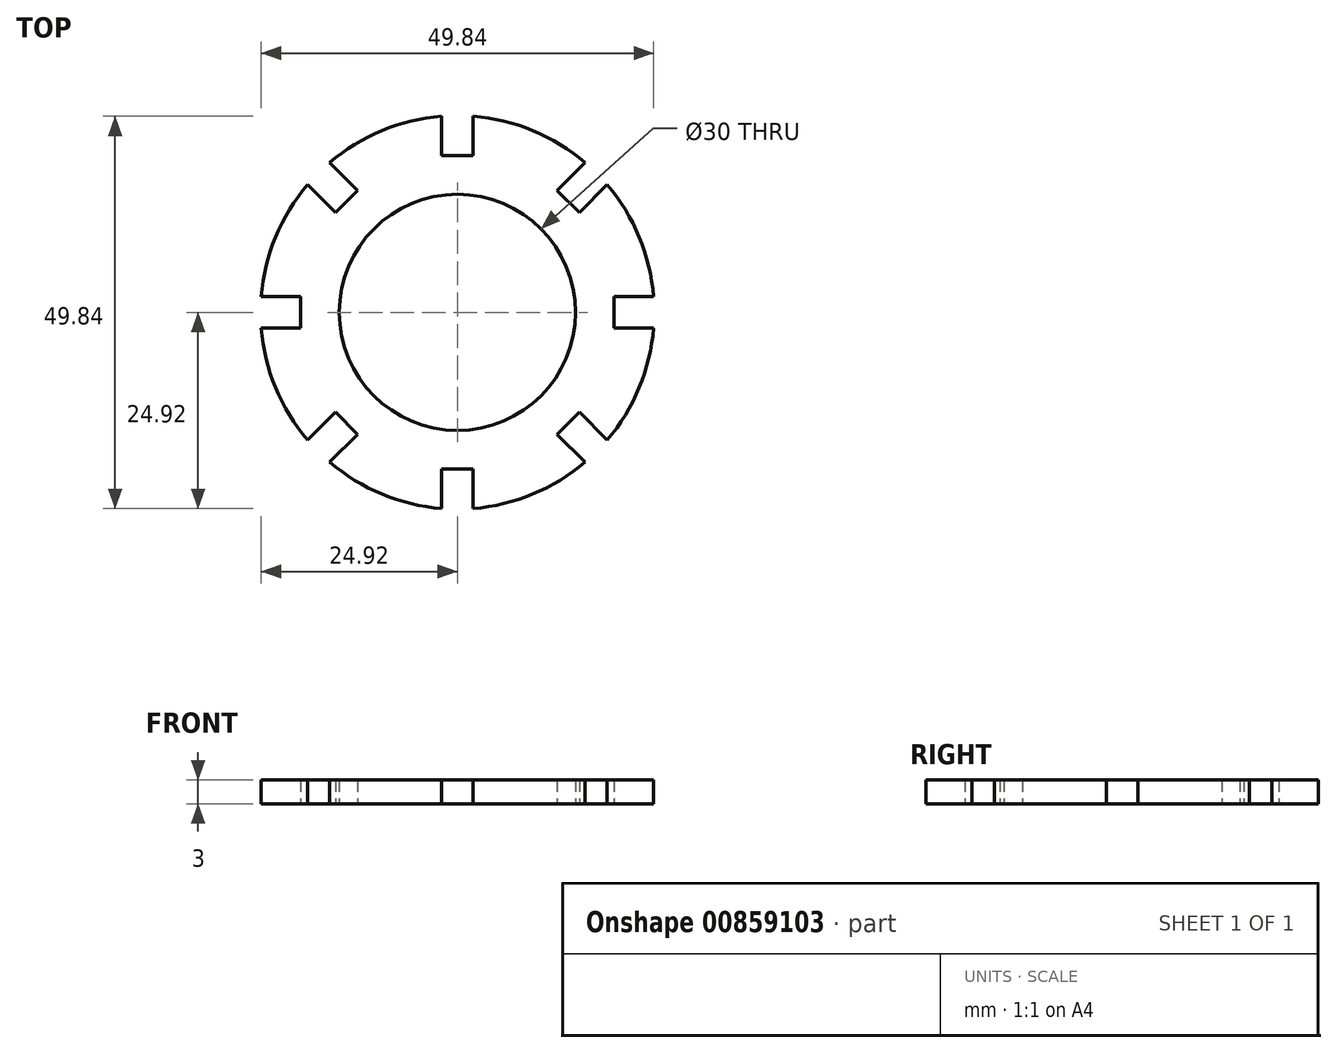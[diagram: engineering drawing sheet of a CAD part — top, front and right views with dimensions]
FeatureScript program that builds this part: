
annotation { "Feature Type Name" : "Feature", "Feature Type Description" : "" }
export const myFeature = defineFeature(function(context is Context, id is Id, definition is map)
    precondition{}
    {
        {
            var Q0;
            Q0=qCreatedBy(makeId("Top.planeOp"),FACE);
            var sketch = newSketch(context, id + "F0", { "sketchPlane" : qUnion([Q0])});
            skCircle(sketch, "E0", {"center": v(0, 0) * mm, "radius": 25 * mm});
            skCircle(sketch, "E1", {"center": v(0, 0) * mm, "radius": 15 * mm});
            skLineSegment(sketch, "E2", {"start": v(0, -19.92) * mm, "end": v(2, -19.92) * mm});
            skLineSegment(sketch, "E3", {"start": v(2, -19.92) * mm, "end": v(0, -19.92) * mm});
            skLineSegment(sketch, "E4", {"start": v(0, -19.92) * mm, "end": v(-2, -19.92) * mm});
            skLineSegment(sketch, "E5", {"start": v(-2, -19.92) * mm, "end": v(-2, -24.92) * mm});
            skLineSegment(sketch, "E6", {"start": v(2, -19.92) * mm, "end": v(2, -24.92) * mm});
            skLineSegment(sketch, "E7.1.0", {"start": v(12.67, -15.5) * mm, "end": v(16.2, -19.04) * mm});
            skLineSegment(sketch, "E7.1.1", {"start": v(14.09, -14.09) * mm, "end": v(12.67, -15.5) * mm});
            skLineSegment(sketch, "E7.1.2", {"start": v(15.5, -12.67) * mm, "end": v(14.09, -14.09) * mm});
            skLineSegment(sketch, "E7.1.3", {"start": v(15.5, -12.67) * mm, "end": v(19.04, -16.2) * mm});
            skLineSegment(sketch, "E7.2.0", {"start": v(19.92, -2) * mm, "end": v(24.92, -2) * mm});
            skLineSegment(sketch, "E7.2.1", {"start": v(19.92, 0) * mm, "end": v(19.92, -2) * mm});
            skLineSegment(sketch, "E7.2.2", {"start": v(19.92, 2) * mm, "end": v(19.92, 0) * mm});
            skLineSegment(sketch, "E7.2.3", {"start": v(19.92, 2) * mm, "end": v(24.92, 2) * mm});
            skLineSegment(sketch, "E7.3.0", {"start": v(15.5, 12.67) * mm, "end": v(19.04, 16.2) * mm});
            skLineSegment(sketch, "E7.3.1", {"start": v(14.09, 14.09) * mm, "end": v(15.5, 12.67) * mm});
            skLineSegment(sketch, "E7.3.2", {"start": v(12.67, 15.5) * mm, "end": v(14.09, 14.09) * mm});
            skLineSegment(sketch, "E7.3.3", {"start": v(12.67, 15.5) * mm, "end": v(16.2, 19.04) * mm});
            skLineSegment(sketch, "E7.4.0", {"start": v(2, 19.92) * mm, "end": v(2, 24.92) * mm});
            skLineSegment(sketch, "E7.4.1", {"start": v(0, 19.92) * mm, "end": v(2, 19.92) * mm});
            skLineSegment(sketch, "E7.4.2", {"start": v(-2, 19.92) * mm, "end": v(0, 19.92) * mm});
            skLineSegment(sketch, "E7.4.3", {"start": v(-2, 19.92) * mm, "end": v(-2, 24.92) * mm});
            skLineSegment(sketch, "E7.5.0", {"start": v(-12.67, 15.5) * mm, "end": v(-16.2, 19.04) * mm});
            skLineSegment(sketch, "E7.5.1", {"start": v(-14.09, 14.09) * mm, "end": v(-12.67, 15.5) * mm});
            skLineSegment(sketch, "E7.5.2", {"start": v(-15.5, 12.67) * mm, "end": v(-14.09, 14.09) * mm});
            skLineSegment(sketch, "E7.5.3", {"start": v(-15.5, 12.67) * mm, "end": v(-19.04, 16.2) * mm});
            skLineSegment(sketch, "E7.6.0", {"start": v(-19.92, 2) * mm, "end": v(-24.92, 2) * mm});
            skLineSegment(sketch, "E7.6.1", {"start": v(-19.92, 0) * mm, "end": v(-19.92, 2) * mm});
            skLineSegment(sketch, "E7.6.2", {"start": v(-19.92, -2) * mm, "end": v(-19.92, 0) * mm});
            skLineSegment(sketch, "E7.6.3", {"start": v(-19.92, -2) * mm, "end": v(-24.92, -2) * mm});
            skLineSegment(sketch, "E7.7.0", {"start": v(-15.5, -12.67) * mm, "end": v(-19.04, -16.2) * mm});
            skLineSegment(sketch, "E7.7.1", {"start": v(-14.09, -14.09) * mm, "end": v(-15.5, -12.67) * mm});
            skLineSegment(sketch, "E7.7.2", {"start": v(-12.67, -15.5) * mm, "end": v(-14.09, -14.09) * mm});
            skLineSegment(sketch, "E7.7.3", {"start": v(-12.67, -15.5) * mm, "end": v(-16.2, -19.04) * mm});
            skSolve(sketch);
        }
        {
            var Q0;
            Q0=makeQuery(id+"F0.imprint","IMPRINT",FACE,{"disambiguationData":[TD([[makeQuery(id+"F0.imprint","IMPRINT",EDGE,{"derivedFrom":sQuery(id+"F0.wireOp",EDGE,"E1")}),-1.0]])]});
            extrude(context, id + "F1", {"entities" : qUnion([Q0]), "depth" : 3 * mm, "offsetDistance" : 25 * mm});
        }
    });
